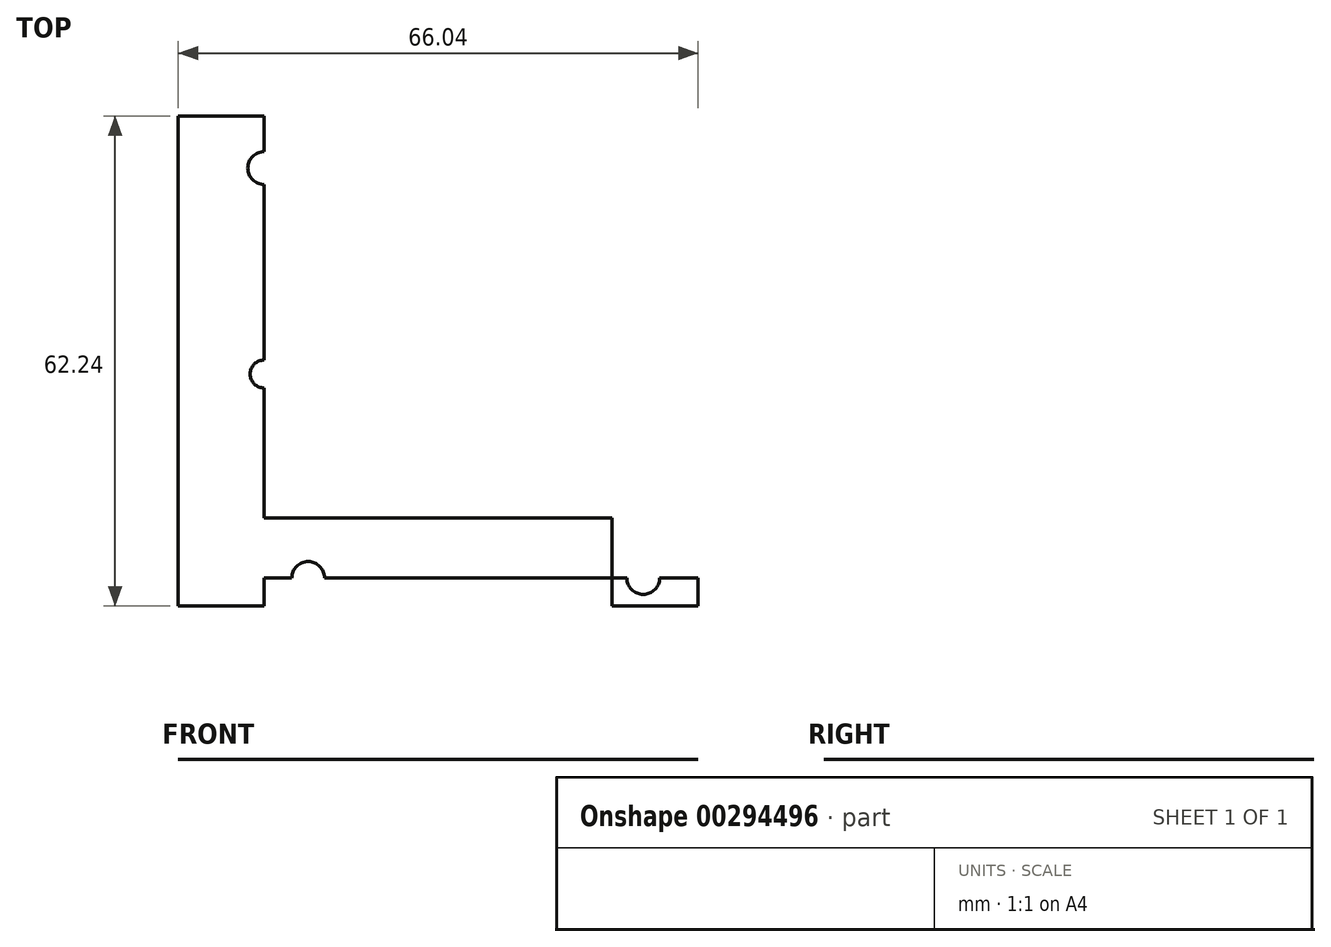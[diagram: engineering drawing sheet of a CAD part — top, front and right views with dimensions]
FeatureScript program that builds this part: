
annotation { "Feature Type Name" : "Feature", "Feature Type Description" : "" }
export const myFeature = defineFeature(function(context is Context, id is Id, definition is map)
    precondition{}
    {
        {
            var Q0;
            Q0=qCreatedBy(makeId("Top.planeOp"),FACE);
            var sketch = newSketch(context, id + "F0", { "sketchPlane" : qUnion([Q0])});
            skLineSegment(sketch, "E0.bottom", {"start": v(33.02, 31.12) * mm, "end": v(-33.02, 31.12) * mm});
            skLineSegment(sketch, "E0.top", {"start": v(33.02, -31.12) * mm, "end": v(-33.02, -31.12) * mm});
            skLineSegment(sketch, "E0.left", {"start": v(33.02, 31.12) * mm, "end": v(33.02, -31.12) * mm});
            skLineSegment(sketch, "E0.right", {"start": v(-33.02, 31.12) * mm, "end": v(-33.02, -31.12) * mm});
            skPoint(sketch, "E0.middle", {"position": v(0, 0) * mm});
            skLineSegment(sketch, "E1.bottom", {"start": v(22.1, 31.12) * mm, "end": v(-22.1, 31.12) * mm});
            skLineSegment(sketch, "E1.top", {"start": v(22.1, -31.12) * mm, "end": v(-22.1, -31.12) * mm});
            skLineSegment(sketch, "E1.left", {"start": v(22.1, 31.11) * mm, "end": v(22.1, -31.12) * mm});
            skLineSegment(sketch, "E1.right", {"start": v(-22.1, 31.11) * mm, "end": v(-22.1, -31.12) * mm});
            skCircle(sketch, "E2", {"center": v(22.1, 24.51) * mm, "radius": 2.08 * mm});
            skCircle(sketch, "E3", {"center": v(22.1, -1.65) * mm, "radius": 2.08 * mm});
            skCircle(sketch, "E4", {"center": v(-22.1, 24.51) * mm, "radius": 2.08 * mm});
            skCircle(sketch, "E5", {"center": v(-22.1, -1.65) * mm, "radius": 1.78 * mm});
            skLineSegment(sketch, "E6.bottom", {"start": v(-22.1, -9.78) * mm, "end": v(22.1, -9.78) * mm});
            skLineSegment(sketch, "E6.top", {"start": v(-22.1, -19.94) * mm, "end": v(22.1, -19.94) * mm});
            skLineSegment(sketch, "E6.left", {"start": v(-22.1, -9.78) * mm, "end": v(-22.1, -19.94) * mm});
            skLineSegment(sketch, "E6.right", {"start": v(22.1, -9.78) * mm, "end": v(22.1, -19.94) * mm});
            skLineSegment(sketch, "E7", {"start": v(-22.1, -27.56) * mm, "end": v(33.02, -27.56) * mm});
            skCircle(sketch, "E8", {"center": v(-16.51, -27.56) * mm, "radius": 2.08 * mm});
            skCircle(sketch, "E9", {"center": v(26.05, -27.56) * mm, "radius": 2.08 * mm});
            skLineSegment(sketch, "E10", {"start": v(0, 0) * mm, "end": v(0, 31.12) * mm});
            skSolve(sketch);
        }
        {
            var Q0;
            {var subQ9=sQuery(id+"F0.wireOp",EDGE,"E1.bottom");Q0=makeQuery(id+"F0.imprint","IMPRINT",FACE,{"disambiguationData":[TD([[makeQuery(id+"F0.imprint","IMPRINT",EDGE,{"derivedFrom":subQ9}),1.0]])]});}
            var Q1;
            {var subQ0=sQuery(id+"F0.wireOp",EDGE,"E0.right");Q1=makeQuery(id+"F0.imprint","IMPRINT",FACE,{"disambiguationData":[TD([[makeQuery(id+"F0.imprint","IMPRINT",EDGE,{"derivedFrom":subQ0}),1.0]])]});}
            var Q2;
            {var subQ6=sQuery(id+"F0.wireOp",EDGE,"E0.left");Q2=makeQuery(id+"F0.imprint","IMPRINT",FACE,{"disambiguationData":[TD([[makeQuery(id+"F0.imprint","IMPRINT",EDGE,{"derivedFrom":subQ6}),-1.0]])]});}
            var Q3;
            {var subQ5=sQuery(id+"F0.wireOp",EDGE,"E6.top");Q3=makeQuery(id+"F0.imprint","IMPRINT",FACE,{"disambiguationData":[TD([[makeQuery(id+"F0.imprint","IMPRINT",EDGE,{"derivedFrom":subQ5}),-1.0]])]});}
            var Q4;
            {var subQ1=sQuery(id+"F0.wireOp",EDGE,"E1.top");Q4=makeQuery(id+"F0.imprint","IMPRINT",FACE,{"disambiguationData":[TD([[makeQuery(id+"F0.imprint","IMPRINT",EDGE,{"derivedFrom":subQ1}),-1.0]])]});}
            var Q5;
            {var subQ5=sQuery(id+"F0.wireOp",EDGE,"E6.right");Q5=makeQuery(id+"F0.imprint","IMPRINT",FACE,{"disambiguationData":[TD([[makeQuery(id+"F0.imprint","IMPRINT",EDGE,{"derivedFrom":subQ5}),1.0]])]});}
            extrude(context, id + "F1", {"entities" : qUnion([Q0, Q1, Q2, Q3, Q4, Q5]), "depth" : 1 / 406.4 * mm});
        }
    });
